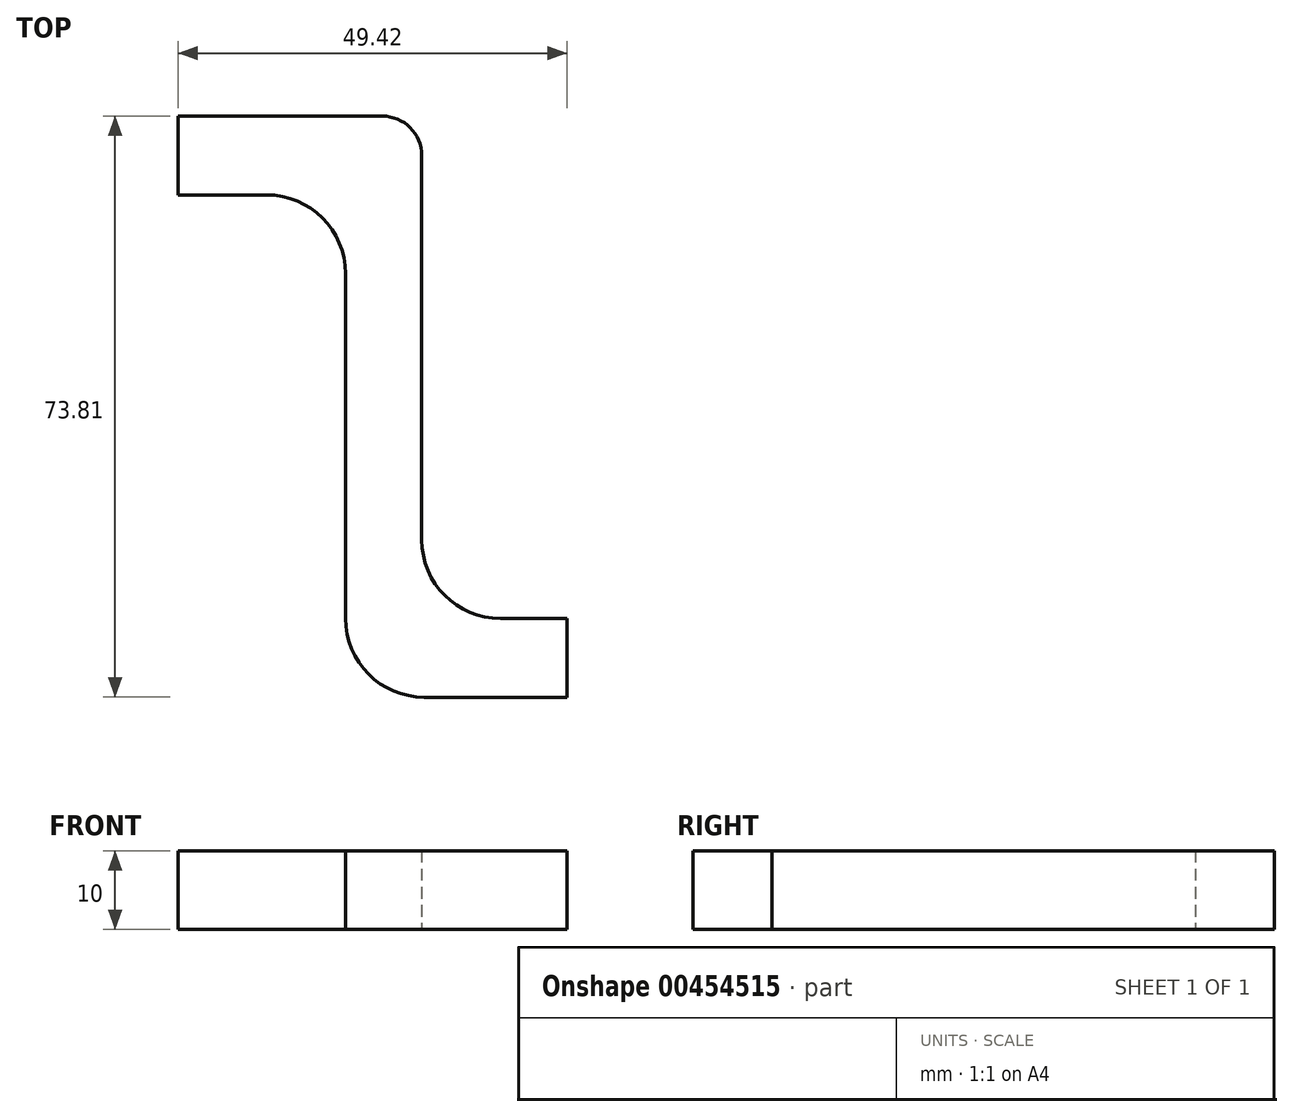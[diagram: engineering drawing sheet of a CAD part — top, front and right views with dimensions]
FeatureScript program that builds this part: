
annotation { "Feature Type Name" : "Feature", "Feature Type Description" : "" }
export const myFeature = defineFeature(function(context is Context, id is Id, definition is map)
    precondition{}
    {
        {
            var Q0;
            Q0=qCreatedBy(makeId("Top.planeOp"),FACE);
            var sketch = newSketch(context, id + "F0", { "sketchPlane" : qUnion([Q0])});
            skLineSegment(sketch, "E0.bottom", {"start": v(-13.83, 35.55) * mm, "end": v(-3.83, 35.55) * mm});
            skLineSegment(sketch, "E0.top", {"start": v(1.48, -38.26) * mm, "end": v(2.9, -38.26) * mm});
            skLineSegment(sketch, "E0.left", {"start": v(-8.52, 15.55) * mm, "end": v(-8.52, -28.26) * mm});
            skLineSegment(sketch, "E0.right", {"start": v(1.17, 30.55) * mm, "end": v(1.17, -18.26) * mm});
            skLineSegment(sketch, "E1.bottom", {"start": v(2.9, -38.26) * mm, "end": v(19.64, -38.26) * mm});
            skLineSegment(sketch, "E1.top", {"start": v(11.17, -28.26) * mm, "end": v(19.64, -28.26) * mm});
            skLineSegment(sketch, "E1.right", {"start": v(19.64, -38.26) * mm, "end": v(19.64, -28.26) * mm});
            skLineSegment(sketch, "E2.bottom", {"start": v(-13.83, 35.55) * mm, "end": v(-29.78, 35.55) * mm});
            skLineSegment(sketch, "E2.top", {"start": v(-18.52, 25.55) * mm, "end": v(-29.78, 25.55) * mm});
            skLineSegment(sketch, "E2.right", {"start": v(-29.78, 35.55) * mm, "end": v(-29.78, 25.55) * mm});
            skPoint(sketch, "E3.visualSharp", {"position": v(1.17, 35.55) * mm});
            skArc(sketch, "E3.filletArc", {"start": v(1.17, 30.55) * mm, "mid": v(-0.3, 34.09) * mm, "end": v(-3.83, 35.55) * mm});
            skPoint(sketch, "E4.visualSharp", {"position": v(-8.52, -38.26) * mm});
            skArc(sketch, "E4.filletArc", {"start": v(-8.52, -28.26) * mm, "mid": v(-5.59, -35.34) * mm, "end": v(1.48, -38.26) * mm});
            skPoint(sketch, "E5.newPointA", {"position": v(-9.78, 25.55) * mm});
            skArc(sketch, "E5.filletArc", {"start": v(-8.52, 15.55) * mm, "mid": v(-11.44, 22.62) * mm, "end": v(-18.52, 25.55) * mm});
            skPoint(sketch, "E6.newPointB", {"position": v(1.17, -39.45) * mm});
            skArc(sketch, "E6.filletArc", {"start": v(1.17, -18.26) * mm, "mid": v(4.1, -25.34) * mm, "end": v(11.17, -28.26) * mm});
            skSolve(sketch);
        }
        {
            var Q0;
            Q0 = qSketchRegion(id + "F0", true);
            extrude(context, id + "F1", {"entities" : qUnion([Q0]), "depth" : 10 * mm});
        }
        {
            var Q0;
            Q0=qCreatedBy(makeId("Top.planeOp"),FACE);
            cPlane(context, id + "F2", {"entities" : qUnion([Q0]), "cplaneType" : CPlaneType.OFFSET, "offset" : 1.22 * mm, "width" : 150 * mm, "height" : 150 * mm});
        }
    });
